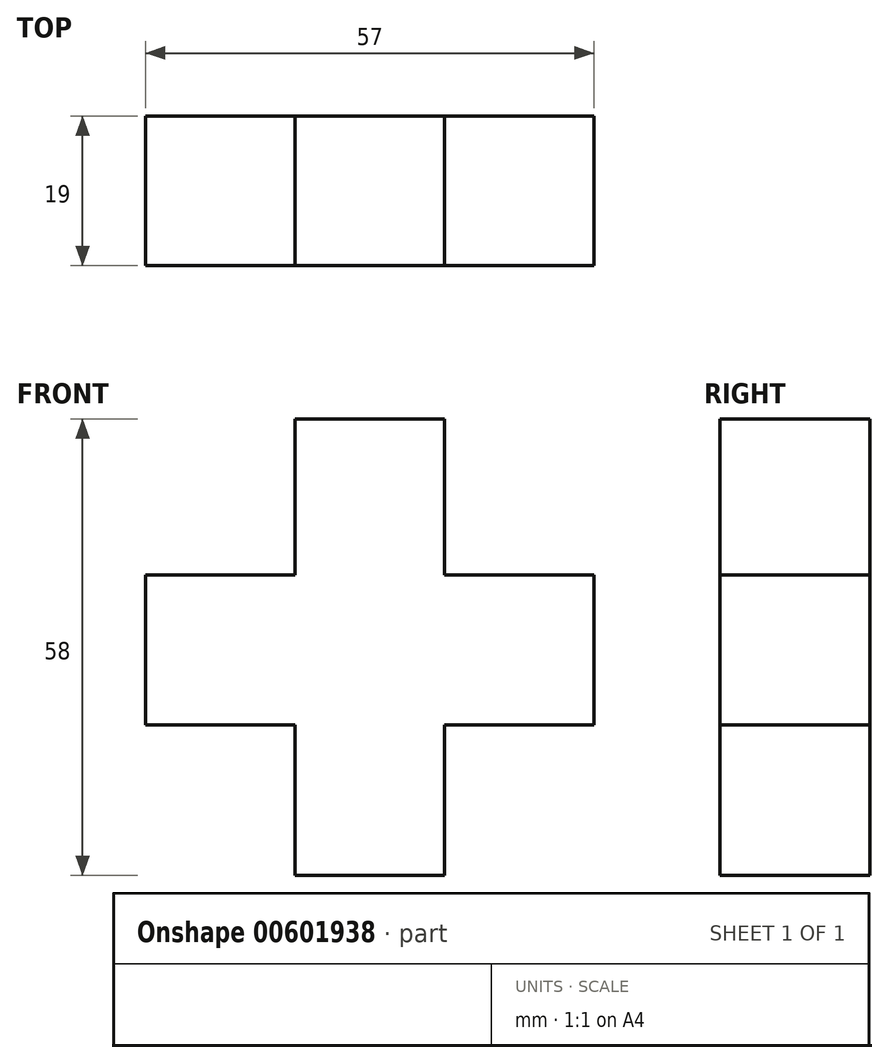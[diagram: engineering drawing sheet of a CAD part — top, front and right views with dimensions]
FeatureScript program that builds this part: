
annotation { "Feature Type Name" : "Feature", "Feature Type Description" : "" }
export const myFeature = defineFeature(function(context is Context, id is Id, definition is map)
    precondition{}
    {
        {
            var Q0;
            Q0=qCreatedBy(makeId("Front.planeOp"),FACE);
            var sketch = newSketch(context, id + "F0", { "sketchPlane" : qUnion([Q0])});
            skLineSegment(sketch, "E0", {"start": v(-11.83, 19.84) * mm, "end": v(7.17, 19.84) * mm});
            skLineSegment(sketch, "E1", {"start": v(7.17, 19.84) * mm, "end": v(7.17, -38.16) * mm});
            skLineSegment(sketch, "E2", {"start": v(7.17, -38.16) * mm, "end": v(-11.83, -38.16) * mm});
            skLineSegment(sketch, "E3", {"start": v(-11.83, -38.16) * mm, "end": v(-11.83, 19.84) * mm});
            skLineSegment(sketch, "E4", {"start": v(7.17, 19.84) * mm, "end": v(7.17, 0) * mm});
            skLineSegment(sketch, "E5", {"start": v(7.17, 0) * mm, "end": v(26.17, 0) * mm});
            skLineSegment(sketch, "E6", {"start": v(26.17, 0) * mm, "end": v(26.17, -19) * mm});
            skLineSegment(sketch, "E7", {"start": v(26.17, -19) * mm, "end": v(7.17, -19) * mm});
            skLineSegment(sketch, "E8", {"start": v(-2.33, -38.16) * mm, "end": v(7.17, -38.16) * mm});
            skLineSegment(sketch, "E9", {"start": v(-11.83, -19) * mm, "end": v(-30.83, -19) * mm});
            skLineSegment(sketch, "E10", {"start": v(-30.83, -19) * mm, "end": v(-30.83, 0) * mm});
            skLineSegment(sketch, "E11", {"start": v(-11.83, 0) * mm, "end": v(-30.83, 0) * mm});
            skSolve(sketch);
        }
        {
            var Q0;
            Q0 = qSketchRegion(id + "F0", true);
            extrude(context, id + "F1", {"entities" : qUnion([Q0]), "depth" : 19 * mm, "offsetDistance" : 25.4 * mm});
        }
    });
